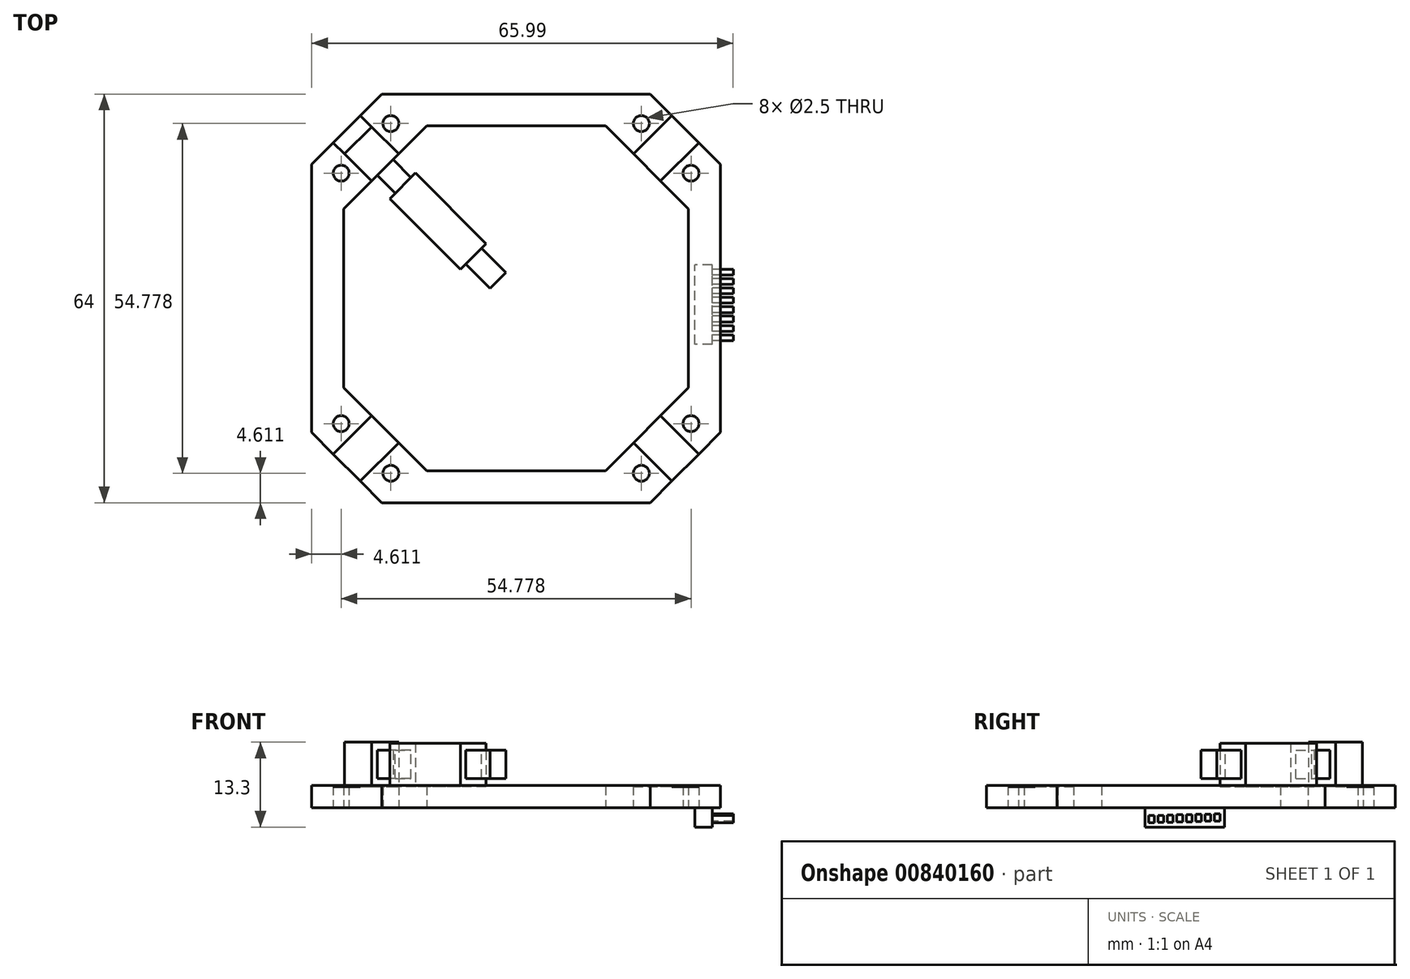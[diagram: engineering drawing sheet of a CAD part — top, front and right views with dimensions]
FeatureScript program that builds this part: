
annotation { "Feature Type Name" : "Feature", "Feature Type Description" : "" }
export const myFeature = defineFeature(function(context is Context, id is Id, definition is map)
    precondition{}
    {
        {
            var Q0;
            Q0=qCreatedBy(makeId("Top.planeOp"),FACE);
            var sketch = newSketch(context, id + "F0", { "sketchPlane" : qUnion([Q0])});
            skLineSegment(sketch, "E0.bottom", {"start": v(-14, 27) * mm, "end": v(14, 27) * mm});
            skLineSegment(sketch, "E0.left", {"start": v(-27, 14) * mm, "end": v(-27, -14) * mm});
            skLineSegment(sketch, "E0.right", {"start": v(27, 14) * mm, "end": v(27, -14) * mm});
            skPoint(sketch, "E0.middle", {"position": v(0, 0) * mm});
            skLineSegment(sketch, "E1.bottom", {"start": v(-21, 32) * mm, "end": v(21, 32) * mm});
            skLineSegment(sketch, "E1.top", {"start": v(-21, -32) * mm, "end": v(21, -32) * mm});
            skLineSegment(sketch, "E1.left", {"start": v(-32, 21) * mm, "end": v(-32, -21) * mm});
            skLineSegment(sketch, "E1.right", {"start": v(32, 21) * mm, "end": v(32, -21) * mm});
            skPoint(sketch, "E2", {"position": v(-21, 32) * mm});
            skPoint(sketch, "E3", {"position": v(-32, 21) * mm});
            skPoint(sketch, "E4", {"position": v(-27, 14) * mm});
            skPoint(sketch, "E5", {"position": v(-14, 27) * mm});
            skPoint(sketch, "E6", {"position": v(-27, 0) * mm});
            skPoint(sketch, "E7", {"position": v(-32, 0) * mm});
            skPoint(sketch, "E8", {"position": v(27, 0) * mm});
            skPoint(sketch, "E9", {"position": v(32, 0) * mm});
            skPoint(sketch, "E10", {"position": v(0, 27) * mm});
            skPoint(sketch, "E11", {"position": v(0, 32) * mm});
            skLineSegment(sketch, "E12", {"start": v(-21, 32) * mm, "end": v(-32, 21) * mm});
            skLineSegment(sketch, "E13", {"start": v(-14, 27) * mm, "end": v(-27, 14) * mm});
            skPoint(sketch, "E14", {"position": v(-27.39, 19.61) * mm});
            skPoint(sketch, "E15", {"position": v(-19.61, 27.39) * mm});
            skCircle(sketch, "E16", {"center": v(-27.39, 19.61) * mm, "radius": 1.25 * mm});
            skCircle(sketch, "E17", {"center": v(-19.61, 27.39) * mm, "radius": 1.25 * mm});
            skPoint(sketch, "E18.1.0", {"position": v(0, -27) * mm});
            skPoint(sketch, "E18.1.1", {"position": v(-26.5, -26.5) * mm});
            skPoint(sketch, "E18.1.4", {"position": v(0, -32) * mm});
            skPoint(sketch, "E18.1.5", {"position": v(-23.5, -23.5) * mm});
            skPoint(sketch, "E18.1.6", {"position": v(-24.39, -16.61) * mm});
            skPoint(sketch, "E18.1.7", {"position": v(-22.61, -30.39) * mm});
            skPoint(sketch, "E18.1.8", {"position": v(-16.61, -24.39) * mm});
            skPoint(sketch, "E18.1.9", {"position": v(-30.39, -22.61) * mm});
            skPoint(sketch, "E18.1.10", {"position": v(-14, -27) * mm});
            skPoint(sketch, "E18.1.12", {"position": v(-27.39, -19.61) * mm});
            skPoint(sketch, "E18.1.13", {"position": v(-21, -32) * mm});
            skPoint(sketch, "E18.1.14", {"position": v(-32, -21) * mm});
            skPoint(sketch, "E18.1.15", {"position": v(-18.38, -22.62) * mm});
            skPoint(sketch, "E18.1.17", {"position": v(-19.61, -27.39) * mm});
            skPoint(sketch, "E18.1.19", {"position": v(-27, -14) * mm});
            skPoint(sketch, "E18.1.20", {"position": v(-20.5, -20.5) * mm});
            skLineSegment(sketch, "E18.1.21", {"start": v(-32, -21) * mm, "end": v(-21, -32) * mm});
            skCircle(sketch, "E18.1.22", {"center": v(-19.61, -27.39) * mm, "radius": 1.25 * mm});
            skCircle(sketch, "E18.1.23", {"center": v(-27.39, -19.61) * mm, "radius": 1.25 * mm});
            skLineSegment(sketch, "E18.1.25", {"start": v(-27, -14) * mm, "end": v(-14, -27) * mm});
            skPoint(sketch, "E18.2.1", {"position": v(26.5, -26.5) * mm});
            skPoint(sketch, "E18.2.3", {"position": v(0, -32) * mm});
            skPoint(sketch, "E18.2.5", {"position": v(23.5, -23.5) * mm});
            skPoint(sketch, "E18.2.6", {"position": v(16.61, -24.39) * mm});
            skPoint(sketch, "E18.2.7", {"position": v(30.39, -22.61) * mm});
            skPoint(sketch, "E18.2.8", {"position": v(24.39, -16.61) * mm});
            skPoint(sketch, "E18.2.9", {"position": v(22.61, -30.39) * mm});
            skPoint(sketch, "E18.2.10", {"position": v(27, -14) * mm});
            skPoint(sketch, "E18.2.11", {"position": v(0, -27) * mm});
            skPoint(sketch, "E18.2.12", {"position": v(19.61, -27.39) * mm});
            skPoint(sketch, "E18.2.13", {"position": v(32, -21) * mm});
            skPoint(sketch, "E18.2.14", {"position": v(21, -32) * mm});
            skPoint(sketch, "E18.2.15", {"position": v(22.62, -18.38) * mm});
            skPoint(sketch, "E18.2.17", {"position": v(27.39, -19.61) * mm});
            skPoint(sketch, "E18.2.19", {"position": v(14, -27) * mm});
            skPoint(sketch, "E18.2.20", {"position": v(20.5, -20.5) * mm});
            skLineSegment(sketch, "E18.2.21", {"start": v(21, -32) * mm, "end": v(32, -21) * mm});
            skCircle(sketch, "E18.2.22", {"center": v(27.39, -19.61) * mm, "radius": 1.25 * mm});
            skCircle(sketch, "E18.2.23", {"center": v(19.61, -27.39) * mm, "radius": 1.25 * mm});
            skLineSegment(sketch, "E18.2.25", {"start": v(14, -27) * mm, "end": v(27, -14) * mm});
            skPoint(sketch, "E18.3.1", {"position": v(26.5, 26.5) * mm});
            skPoint(sketch, "E18.3.10", {"position": v(14, 27) * mm});
            skPoint(sketch, "E18.3.12", {"position": v(27.39, 19.61) * mm});
            skPoint(sketch, "E18.3.13", {"position": v(21, 32) * mm});
            skPoint(sketch, "E18.3.14", {"position": v(32, 21) * mm});
            skPoint(sketch, "E18.3.17", {"position": v(19.61, 27.39) * mm});
            skPoint(sketch, "E18.3.19", {"position": v(27, 14) * mm});
            skPoint(sketch, "E18.3.20", {"position": v(20.5, 20.5) * mm});
            skLineSegment(sketch, "E18.3.21", {"start": v(32, 21) * mm, "end": v(21, 32) * mm});
            skCircle(sketch, "E18.3.22", {"center": v(19.61, 27.39) * mm, "radius": 1.25 * mm});
            skCircle(sketch, "E18.3.23", {"center": v(27.39, 19.61) * mm, "radius": 1.25 * mm});
            skLineSegment(sketch, "E18.3.25", {"start": v(27, 14) * mm, "end": v(14, 27) * mm});
            skLineSegment(sketch, "E19.trimOffspring", {"start": v(-14, -27) * mm, "end": v(14, -27) * mm});
            skPoint(sketch, "E20", {"position": v(-26.5, 26.5) * mm});
            skPoint(sketch, "E21", {"position": v(-20.5, 20.5) * mm});
            skLineSegment(sketch, "E22", {"start": v(-24.38, 28.62) * mm, "end": v(-18.38, 22.62) * mm});
            skLineSegment(sketch, "E23", {"start": v(-28.62, 24.38) * mm, "end": v(-22.62, 18.38) * mm});
            skLineSegment(sketch, "E24.1.0", {"start": v(-28.62, -24.38) * mm, "end": v(-22.62, -18.38) * mm});
            skLineSegment(sketch, "E24.1.1", {"start": v(-24.38, -28.62) * mm, "end": v(-18.38, -22.62) * mm});
            skLineSegment(sketch, "E24.2.0", {"start": v(24.38, -28.62) * mm, "end": v(18.38, -22.62) * mm});
            skLineSegment(sketch, "E24.2.1", {"start": v(28.62, -24.38) * mm, "end": v(22.62, -18.38) * mm});
            skLineSegment(sketch, "E24.3.0", {"start": v(28.62, 24.38) * mm, "end": v(22.62, 18.38) * mm});
            skLineSegment(sketch, "E24.3.1", {"start": v(24.38, 28.62) * mm, "end": v(18.38, 22.62) * mm});
            skSolve(sketch);
        }
        {
            var Q0;
            {var subQ0=sQuery(id+"F0.wireOp",EDGE,"E22");Q0=makeQuery(id+"F0.imprint","IMPRINT",FACE,{"disambiguationData":[TD([[makeQuery(id+"F0.imprint","IMPRINT",EDGE,{"derivedFrom":subQ0}),-1.0]])]});}
            var Q1;
            {var subQ0=sQuery(id+"F0.wireOp",EDGE,"E24.3.0");Q1=makeQuery(id+"F0.imprint","IMPRINT",FACE,{"disambiguationData":[TD([[makeQuery(id+"F0.imprint","IMPRINT",EDGE,{"derivedFrom":subQ0}),-1.0]])]});}
            var Q2;
            {var subQ0=sQuery(id+"F0.wireOp",EDGE,"E24.2.0");Q2=makeQuery(id+"F0.imprint","IMPRINT",FACE,{"disambiguationData":[TD([[makeQuery(id+"F0.imprint","IMPRINT",EDGE,{"derivedFrom":subQ0}),-1.0]])]});}
            var Q3;
            {var subQ0=sQuery(id+"F0.wireOp",EDGE,"E24.1.0");Q3=makeQuery(id+"F0.imprint","IMPRINT",FACE,{"disambiguationData":[TD([[makeQuery(id+"F0.imprint","IMPRINT",EDGE,{"derivedFrom":subQ0}),-1.0]])]});}
            extrude(context, id + "F1", {"entities" : qUnion([Q0, Q1, Q2, Q3]), "depth" : 3.3 * mm, "offsetDistance" : 25 * mm});
        }
        {
            var Q0;
            {var subQ1=sQuery(id+"F0.wireOp",EDGE,"E0.left");Q0=makeQuery(id+"F0.imprint","IMPRINT",FACE,{"disambiguationData":[TD([[makeQuery(id+"F0.imprint","IMPRINT",EDGE,{"derivedFrom":subQ1}),-1.0]])]});}
            var Q1;
            {var subQ5=sQuery(id+"F0.wireOp",EDGE,"E0.bottom");Q1=makeQuery(id+"F0.imprint","IMPRINT",FACE,{"disambiguationData":[TD([[makeQuery(id+"F0.imprint","IMPRINT",EDGE,{"derivedFrom":subQ5}),1.0]])]});}
            var Q2;
            {var subQ4=sQuery(id+"F0.wireOp",EDGE,"E0.right");Q2=makeQuery(id+"F0.imprint","IMPRINT",FACE,{"disambiguationData":[TD([[makeQuery(id+"F0.imprint","IMPRINT",EDGE,{"derivedFrom":subQ4}),1.0]])]});}
            var Q3;
            {var subQ5=sQuery(id+"F0.wireOp",EDGE,"E1.top");Q3=makeQuery(id+"F0.imprint","IMPRINT",FACE,{"disambiguationData":[TD([[makeQuery(id+"F0.imprint","IMPRINT",EDGE,{"derivedFrom":subQ5}),1.0]])]});}
            extrude(context, id + "F2", {"entities" : qUnion([Q0, Q1, Q2, Q3]), "depth" : 3.5 * mm, "offsetDistance" : 25 * mm});
        }
        {
            var Q0;
            Q0=makeQuery(id+"F2.opExtrude","SWEPT_BODY",BODY,{"disambiguationData":[OSD([sQuery(id+"F0.wireOp",EDGE,"E0.left"),sQuery(id+"F0.wireOp",EDGE,"E1.left"),sQuery(id+"F0.wireOp",EDGE,"E12"),sQuery(id+"F0.wireOp",EDGE,"E13"),sQuery(id+"F0.wireOp",EDGE,"E16"),sQuery(id+"F0.wireOp",EDGE,"E18.1.21"),sQuery(id+"F0.wireOp",EDGE,"E18.1.23"),sQuery(id+"F0.wireOp",EDGE,"E18.1.25"),sQuery(id+"F0.wireOp",EDGE,"E23"),sQuery(id+"F0.wireOp",EDGE,"E24.1.0")])]});
            var Q1;
            Q1=makeQuery(id+"F1.opExtrude","SWEPT_BODY",BODY,{"disambiguationData":[OSD([sQuery(id+"F0.wireOp",EDGE,"E18.1.21"),sQuery(id+"F0.wireOp",EDGE,"E18.1.25"),sQuery(id+"F0.wireOp",EDGE,"E24.1.0"),sQuery(id+"F0.wireOp",EDGE,"E24.1.1")])]});
            var Q2;
            Q2=makeQuery(id+"F2.opExtrude","SWEPT_BODY",BODY,{"disambiguationData":[OSD([sQuery(id+"F0.wireOp",EDGE,"E1.top"),sQuery(id+"F0.wireOp",EDGE,"E18.1.21"),sQuery(id+"F0.wireOp",EDGE,"E18.1.22"),sQuery(id+"F0.wireOp",EDGE,"E18.1.25"),sQuery(id+"F0.wireOp",EDGE,"E18.2.21"),sQuery(id+"F0.wireOp",EDGE,"E18.2.23"),sQuery(id+"F0.wireOp",EDGE,"E18.2.25"),sQuery(id+"F0.wireOp",EDGE,"E19.trimOffspring"),sQuery(id+"F0.wireOp",EDGE,"E24.1.1"),sQuery(id+"F0.wireOp",EDGE,"E24.2.0")])]});
            var Q3;
            Q3=makeQuery(id+"F1.opExtrude","SWEPT_BODY",BODY,{"disambiguationData":[OSD([sQuery(id+"F0.wireOp",EDGE,"E18.2.21"),sQuery(id+"F0.wireOp",EDGE,"E18.2.25"),sQuery(id+"F0.wireOp",EDGE,"E24.2.0"),sQuery(id+"F0.wireOp",EDGE,"E24.2.1")])]});
            var Q4;
            Q4=makeQuery(id+"F2.opExtrude","SWEPT_BODY",BODY,{"disambiguationData":[OSD([sQuery(id+"F0.wireOp",EDGE,"E0.right"),sQuery(id+"F0.wireOp",EDGE,"E1.right"),sQuery(id+"F0.wireOp",EDGE,"E18.2.21"),sQuery(id+"F0.wireOp",EDGE,"E18.2.22"),sQuery(id+"F0.wireOp",EDGE,"E18.2.25"),sQuery(id+"F0.wireOp",EDGE,"E18.3.21"),sQuery(id+"F0.wireOp",EDGE,"E18.3.23"),sQuery(id+"F0.wireOp",EDGE,"E18.3.25"),sQuery(id+"F0.wireOp",EDGE,"E24.2.1"),sQuery(id+"F0.wireOp",EDGE,"E24.3.0")])]});
            var Q5;
            Q5=makeQuery(id+"F1.opExtrude","SWEPT_BODY",BODY,{"disambiguationData":[OSD([sQuery(id+"F0.wireOp",EDGE,"E18.3.21"),sQuery(id+"F0.wireOp",EDGE,"E18.3.25"),sQuery(id+"F0.wireOp",EDGE,"E24.3.0"),sQuery(id+"F0.wireOp",EDGE,"E24.3.1")])]});
            var Q6;
            Q6=makeQuery(id+"F2.opExtrude","SWEPT_BODY",BODY,{"disambiguationData":[OSD([sQuery(id+"F0.wireOp",EDGE,"E0.bottom"),sQuery(id+"F0.wireOp",EDGE,"E1.bottom"),sQuery(id+"F0.wireOp",EDGE,"E12"),sQuery(id+"F0.wireOp",EDGE,"E13"),sQuery(id+"F0.wireOp",EDGE,"E17"),sQuery(id+"F0.wireOp",EDGE,"E18.3.21"),sQuery(id+"F0.wireOp",EDGE,"E18.3.22"),sQuery(id+"F0.wireOp",EDGE,"E18.3.25"),sQuery(id+"F0.wireOp",EDGE,"E22"),sQuery(id+"F0.wireOp",EDGE,"E24.3.1")])]});
            var Q7;
            Q7=makeQuery(id+"F1.opExtrude","SWEPT_BODY",BODY,{"disambiguationData":[OSD([sQuery(id+"F0.wireOp",EDGE,"E12"),sQuery(id+"F0.wireOp",EDGE,"E13"),sQuery(id+"F0.wireOp",EDGE,"E22"),sQuery(id+"F0.wireOp",EDGE,"E23")])]});
            booleanBodies(context, id + "F3", {"operationType" : BooleanOperationType.UNION, "tools" : qUnion([Q0, Q1, Q2, Q3, Q4, Q5, Q6, Q7])});
        }
        {
            var Q0;
            Q0=makeQuery(id+"F1.opExtrude","CAP_FACE",FACE,{"disambiguationData":[OSD([sQuery(id+"F0.wireOp",EDGE,"E12"),sQuery(id+"F0.wireOp",EDGE,"E13"),sQuery(id+"F0.wireOp",EDGE,"E22"),sQuery(id+"F0.wireOp",EDGE,"E23")])],"isStart":false});
            var sketch = newSketch(context, id + "F4", { "sketchPlane" : qUnion([Q0])});
            skLineSegment(sketch, "E25", {"start": v(-22.62, 18.38) * mm, "end": v(-18.38, 22.62) * mm});
            skLineSegment(sketch, "E26", {"start": v(-26.86, 22.62) * mm, "end": v(-22.62, 26.86) * mm});
            skSolve(sketch);
        }
        {
            var Q0;
            Q0 = qSketchRegion(id + "F4", true);
            var Q1;
            {var subQ0=sQuery(id+"F4.wireOp",EDGE,"E25");Q1=makeQuery(id+"F4.imprint","IMPRINT",FACE,{"disambiguationData":[TD([[makeQuery(id+"F4.imprint","IMPRINT",EDGE,{"derivedFrom":subQ0}),-1.0]])]});}
            extrude(context, id + "F5", {"entities" : qUnion([Q0, Q1]), "depth" : 7 * mm, "offsetDistance" : 25 * mm});
        }
        {
            var Q0;
            Q0=makeQuery(id+"F5.opExtrude","SWEPT_FACE",FACE,{"disambiguationData":[OSD([sQuery(id+"F4.wireOp",EDGE,"E25")])]});
            var sketch = newSketch(context, id + "F6", { "sketchPlane" : qUnion([Q0])});
            skPoint(sketch, "E27", {"position": v(-3, 6.8) * mm});
            skPoint(sketch, "E28", {"position": v(0, 10.3) * mm});
            skPoint(sketch, "E29", {"position": v(0, 6.8) * mm});
            skPoint(sketch, "E30.orphan", {"position": v(3, 6.8) * mm});
            skPoint(sketch, "E31.end.orphan", {"position": v(0, 3.3) * mm});
            skLineSegment(sketch, "E32.bottom", {"start": v(1.75, 9.02) * mm, "end": v(-1.75, 9.02) * mm});
            skLineSegment(sketch, "E32.top", {"start": v(1.75, 4.58) * mm, "end": v(-1.75, 4.58) * mm});
            skLineSegment(sketch, "E32.left", {"start": v(1.75, 9.02) * mm, "end": v(1.75, 4.58) * mm});
            skLineSegment(sketch, "E32.right", {"start": v(-1.75, 9.02) * mm, "end": v(-1.75, 4.58) * mm});
            skSolve(sketch);
        }
        {
            var Q0;
            Q0=makeQuery(id+"F6.imprint","IMPRINT",FACE,{"disambiguationData":[TD([[makeQuery(id+"F6.imprint","IMPRINT",EDGE,{"derivedFrom":sQuery(id+"F6.wireOp",EDGE,"E32.bottom")}),1.0]])]});
            extrude(context, id + "F7", {"entities" : qUnion([Q0]), "operationType" : NewBodyOperationType.ADD, "depth" : 25 * mm, "offsetDistance" : 25 * mm});
        }
        {
            var Q0;
            Q0=makeQuery(id+"F5.opExtrude","SWEPT_BODY",BODY,{"disambiguationData":[OSD([sQuery(id+"F0.wireOp",EDGE,"E22"),sQuery(id+"F0.wireOp",EDGE,"E23"),sQuery(id+"F4.wireOp",EDGE,"E25"),sQuery(id+"F4.wireOp",EDGE,"E26")])]});
            transform(context, id + "F8", {"entities" : qUnion([Q0]), "transformType" : TransformType.TRANSLATION_3D, "dx" : 0 * mm, "dy" : 0 * mm, "dz" : 0 * mm, "makeCopy" : true});
        }
        {
            var Q0;
            Q0=makeQuery(id+"F5.opExtrude","SWEPT_BODY",BODY,{"disambiguationData":[OSD([sQuery(id+"F0.wireOp",EDGE,"E22"),sQuery(id+"F0.wireOp",EDGE,"E23"),sQuery(id+"F4.wireOp",EDGE,"E25"),sQuery(id+"F4.wireOp",EDGE,"E26")])]});
            deleteBodies(context, id + "F9", {"entities" : qUnion([Q0])});
        }
        {
            var Q0;
            Q0=makeQuery(id+"F8.opPattern","COPY",FACE,{"derivedFrom":makeQuery(id+"F7.opExtrude","SWEPT_FACE",FACE,{"disambiguationData":[OSD([sQuery(id+"F6.wireOp",EDGE,"E32.right")])]}),"instanceName":"1"});
            var sketch = newSketch(context, id + "F10", { "sketchPlane" : qUnion([Q0])});
            skLineSegment(sketch, "E33.bottom", {"start": v(-9.38, 10.14) * mm, "end": v(-25.02, 10.14) * mm});
            skLineSegment(sketch, "E33.top", {"start": v(-9.38, 3.35) * mm, "end": v(-25.02, 3.35) * mm});
            skLineSegment(sketch, "E33.left", {"start": v(-9.38, 10.14) * mm, "end": v(-9.38, 3.35) * mm});
            skLineSegment(sketch, "E33.right", {"start": v(-25.02, 10.14) * mm, "end": v(-25.02, 3.35) * mm});
            skSolve(sketch);
        }
        {
            var Q0;
            Q0 = qSketchRegion(id + "F10", true);
            extrude(context, id + "F11", {"entities" : qUnion([Q0]), "operationType" : NewBodyOperationType.ADD, "oppositeDirection" : true, "depth" : 4.5 * mm, "offsetDistance" : 25 * mm, "hasSecondDirection" : true, "secondDirectionOppositeDirection" : false, "secondDirectionDepth" : 1.2 * mm});
        }
        {
            var Q0;
            {var subQ0=sQuery(id+"F0.wireOp",EDGE,"E24.2.0");var subQ1=sQuery(id+"F0.wireOp",EDGE,"E24.1.1");var subQ2=sQuery(id+"F0.wireOp",EDGE,"E18.2.25");var subQ3=sQuery(id+"F0.wireOp",EDGE,"E18.2.21");var subQ4=sQuery(id+"F0.wireOp",EDGE,"E18.1.25");var subQ5=sQuery(id+"F0.wireOp",EDGE,"E18.1.21");var subQ6=sQuery(id+"F0.wireOp",EDGE,"E24.3.0");var subQ7=sQuery(id+"F0.wireOp",EDGE,"E24.2.1");var subQ8=sQuery(id+"F0.wireOp",EDGE,"E18.3.25");var subQ9=sQuery(id+"F0.wireOp",EDGE,"E18.3.21");var subQ10=sQuery(id+"F0.wireOp",EDGE,"E24.1.0");var subQ11=sQuery(id+"F0.wireOp",EDGE,"E23");var subQ12=sQuery(id+"F0.wireOp",EDGE,"E13");var subQ13=sQuery(id+"F0.wireOp",EDGE,"E12");var subQ14=sQuery(id+"F0.wireOp",EDGE,"E24.3.1");var subQ15=sQuery(id+"F0.wireOp",EDGE,"E22");Q0=makeQuery(id+"F3.opBoolean","MERGE",FACE,{"derivedFrom":[makeQuery(id+"F1.opExtrude","CAP_FACE",FACE,{"disambiguationData":[OSD([subQ13,subQ12,subQ15,subQ11])],"isStart":true}),makeQuery(id+"F1.opExtrude","CAP_FACE",FACE,{"disambiguationData":[OSD([subQ5,subQ4,subQ10,subQ1])],"isStart":true}),makeQuery(id+"F1.opExtrude","CAP_FACE",FACE,{"disambiguationData":[OSD([subQ3,subQ2,subQ0,subQ7])],"isStart":true}),makeQuery(id+"F1.opExtrude","CAP_FACE",FACE,{"disambiguationData":[OSD([subQ9,subQ8,subQ6,subQ14])],"isStart":true}),makeQuery(id+"F2.opExtrude","CAP_FACE",FACE,{"disambiguationData":[OSD([sQuery(id+"F0.wireOp",EDGE,"E0.bottom"),sQuery(id+"F0.wireOp",EDGE,"E1.bottom"),subQ13,subQ12,sQuery(id+"F0.wireOp",EDGE,"E17"),subQ9,sQuery(id+"F0.wireOp",EDGE,"E18.3.22"),subQ8,subQ15,subQ14])],"isStart":true}),makeQuery(id+"F2.opExtrude","CAP_FACE",FACE,{"disambiguationData":[OSD([sQuery(id+"F0.wireOp",EDGE,"E0.left"),sQuery(id+"F0.wireOp",EDGE,"E1.left"),subQ13,subQ12,sQuery(id+"F0.wireOp",EDGE,"E16"),subQ5,sQuery(id+"F0.wireOp",EDGE,"E18.1.23"),subQ4,subQ11,subQ10])],"isStart":true}),makeQuery(id+"F2.opExtrude","CAP_FACE",FACE,{"disambiguationData":[OSD([sQuery(id+"F0.wireOp",EDGE,"E0.right"),sQuery(id+"F0.wireOp",EDGE,"E1.right"),subQ3,sQuery(id+"F0.wireOp",EDGE,"E18.2.22"),subQ2,subQ9,sQuery(id+"F0.wireOp",EDGE,"E18.3.23"),subQ8,subQ7,subQ6])],"isStart":true}),makeQuery(id+"F2.opExtrude","CAP_FACE",FACE,{"disambiguationData":[OSD([sQuery(id+"F0.wireOp",EDGE,"E1.top"),subQ5,sQuery(id+"F0.wireOp",EDGE,"E18.1.22"),subQ4,subQ3,sQuery(id+"F0.wireOp",EDGE,"E18.2.23"),subQ2,sQuery(id+"F0.wireOp",EDGE,"E19.trimOffspring"),subQ1,subQ0])],"isStart":true})]});}
            var sketch = newSketch(context, id + "F12", { "sketchPlane" : qUnion([Q0])});
            skLineSegment(sketch, "E34.bottom", {"start": v(30.7, 7.19) * mm, "end": v(28.01, 7.19) * mm});
            skLineSegment(sketch, "E34.top", {"start": v(30.7, -5.26) * mm, "end": v(28.01, -5.26) * mm});
            skLineSegment(sketch, "E34.left", {"start": v(30.7, 7.19) * mm, "end": v(30.7, -5.26) * mm});
            skLineSegment(sketch, "E34.right", {"start": v(28.01, 7.19) * mm, "end": v(28.01, -5.26) * mm});
            skPoint(sketch, "E34.middle", {"position": v(29.35, 0.96) * mm});
            skSolve(sketch);
        }
        {
            var Q0;
            Q0 = qSketchRegion(id + "F12", true);
            extrude(context, id + "F13", {"entities" : qUnion([Q0]), "depth" : 3 * mm, "offsetDistance" : 25 * mm});
        }
        {
            var Q0;
            Q0=makeQuery(id+"F13.opExtrude","SWEPT_FACE",FACE,{"disambiguationData":[OSD([sQuery(id+"F12.wireOp",EDGE,"E34.left")])]});
            var sketch = newSketch(context, id + "F14", { "sketchPlane" : qUnion([Q0])});
            skLineSegment(sketch, "E35.bottom", {"start": v(3.67, -2.06) * mm, "end": v(4.58, -2.06) * mm});
            skLineSegment(sketch, "E35.top", {"start": v(3.67, -0.94) * mm, "end": v(4.58, -0.94) * mm});
            skLineSegment(sketch, "E35.left", {"start": v(3.67, -2.06) * mm, "end": v(3.67, -0.94) * mm});
            skLineSegment(sketch, "E35.right", {"start": v(4.58, -2.06) * mm, "end": v(4.58, -0.94) * mm});
            skPoint(sketch, "E35.middle", {"position": v(4.12, -1.5) * mm});
            skPoint(sketch, "E35.middle.positionSnap0", {"position": v(5.26, -1.5) * mm});
            skPoint(sketch, "E35.centerSnap0", {"position": v(5.26, -1.5) * mm});
            skLineSegment(sketch, "E36.1.0.0", {"start": v(2.2, -2.1) * mm, "end": v(2.2, -0.97) * mm});
            skLineSegment(sketch, "E36.1.0.1", {"start": v(2.2, -0.97) * mm, "end": v(3.1, -0.97) * mm});
            skLineSegment(sketch, "E36.1.0.2", {"start": v(3.1, -2.1) * mm, "end": v(3.1, -0.97) * mm});
            skLineSegment(sketch, "E36.1.0.3", {"start": v(2.2, -2.1) * mm, "end": v(3.1, -2.1) * mm});
            skLineSegment(sketch, "E36.2.0.0", {"start": v(0.73, -2.14) * mm, "end": v(0.73, -1.01) * mm});
            skLineSegment(sketch, "E36.2.0.1", {"start": v(0.73, -1.01) * mm, "end": v(1.63, -1.01) * mm});
            skLineSegment(sketch, "E36.2.0.2", {"start": v(1.63, -2.14) * mm, "end": v(1.63, -1.01) * mm});
            skLineSegment(sketch, "E36.2.0.3", {"start": v(0.73, -2.14) * mm, "end": v(1.63, -2.14) * mm});
            skLineSegment(sketch, "E36.3.0.0", {"start": v(-0.74, -2.17) * mm, "end": v(-0.74, -1.05) * mm});
            skLineSegment(sketch, "E36.3.0.1", {"start": v(-0.74, -1.05) * mm, "end": v(0.16, -1.05) * mm});
            skLineSegment(sketch, "E36.3.0.2", {"start": v(0.16, -2.17) * mm, "end": v(0.16, -1.05) * mm});
            skLineSegment(sketch, "E36.3.0.3", {"start": v(-0.74, -2.17) * mm, "end": v(0.16, -2.17) * mm});
            skLineSegment(sketch, "E36.4.0.0", {"start": v(-2.22, -2.21) * mm, "end": v(-2.22, -1.09) * mm});
            skLineSegment(sketch, "E36.4.0.1", {"start": v(-2.22, -1.09) * mm, "end": v(-1.3, -1.09) * mm});
            skLineSegment(sketch, "E36.4.0.2", {"start": v(-1.3, -2.21) * mm, "end": v(-1.3, -1.09) * mm});
            skLineSegment(sketch, "E36.4.0.3", {"start": v(-2.22, -2.21) * mm, "end": v(-1.3, -2.21) * mm});
            skLineSegment(sketch, "E36.5.0.0", {"start": v(-3.69, -2.25) * mm, "end": v(-3.69, -1.12) * mm});
            skLineSegment(sketch, "E36.5.0.1", {"start": v(-3.69, -1.12) * mm, "end": v(-2.78, -1.12) * mm});
            skLineSegment(sketch, "E36.5.0.2", {"start": v(-2.78, -2.25) * mm, "end": v(-2.78, -1.12) * mm});
            skLineSegment(sketch, "E36.5.0.3", {"start": v(-3.69, -2.25) * mm, "end": v(-2.78, -2.25) * mm});
            skLineSegment(sketch, "E36.6.0.0", {"start": v(-5.16, -2.29) * mm, "end": v(-5.16, -1.16) * mm});
            skLineSegment(sketch, "E36.6.0.1", {"start": v(-5.16, -1.16) * mm, "end": v(-4.25, -1.16) * mm});
            skLineSegment(sketch, "E36.6.0.2", {"start": v(-4.25, -2.29) * mm, "end": v(-4.25, -1.16) * mm});
            skLineSegment(sketch, "E36.6.0.3", {"start": v(-5.16, -2.29) * mm, "end": v(-4.25, -2.29) * mm});
            skLineSegment(sketch, "E36.7.0.0", {"start": v(-6.63, -2.32) * mm, "end": v(-6.63, -1.2) * mm});
            skLineSegment(sketch, "E36.7.0.1", {"start": v(-6.63, -1.2) * mm, "end": v(-5.72, -1.2) * mm});
            skLineSegment(sketch, "E36.7.0.2", {"start": v(-5.72, -2.32) * mm, "end": v(-5.72, -1.2) * mm});
            skLineSegment(sketch, "E36.7.0.3", {"start": v(-6.63, -2.32) * mm, "end": v(-5.72, -2.32) * mm});
            skLineSegment(sketch, "E36.direction1", {"start": v(3.67, -2.06) * mm, "end": v(2.2, -2.1) * mm, "construction": true});
            skSolve(sketch);
        }
        {
            var Q0;
            Q0=makeQuery(id+"F14.imprint","IMPRINT",FACE,{"disambiguationData":[TD([[makeQuery(id+"F14.imprint","IMPRINT",EDGE,{"derivedFrom":sQuery(id+"F14.wireOp",EDGE,"E36.7.0.0")}),-1.0]])]});
            var Q1;
            Q1=makeQuery(id+"F14.imprint","IMPRINT",FACE,{"disambiguationData":[TD([[makeQuery(id+"F14.imprint","IMPRINT",EDGE,{"derivedFrom":sQuery(id+"F14.wireOp",EDGE,"E36.6.0.0")}),-1.0]])]});
            var Q2;
            Q2=makeQuery(id+"F14.imprint","IMPRINT",FACE,{"disambiguationData":[TD([[makeQuery(id+"F14.imprint","IMPRINT",EDGE,{"derivedFrom":sQuery(id+"F14.wireOp",EDGE,"E36.5.0.0")}),-1.0]])]});
            var Q3;
            Q3 = qSketchRegion(id + "F14", true);
            extrude(context, id + "F15", {"entities" : qUnion([Q0, Q1, Q2, Q3]), "operationType" : NewBodyOperationType.ADD, "depth" : 3.3 * mm, "offsetDistance" : 25 * mm});
        }
    });
